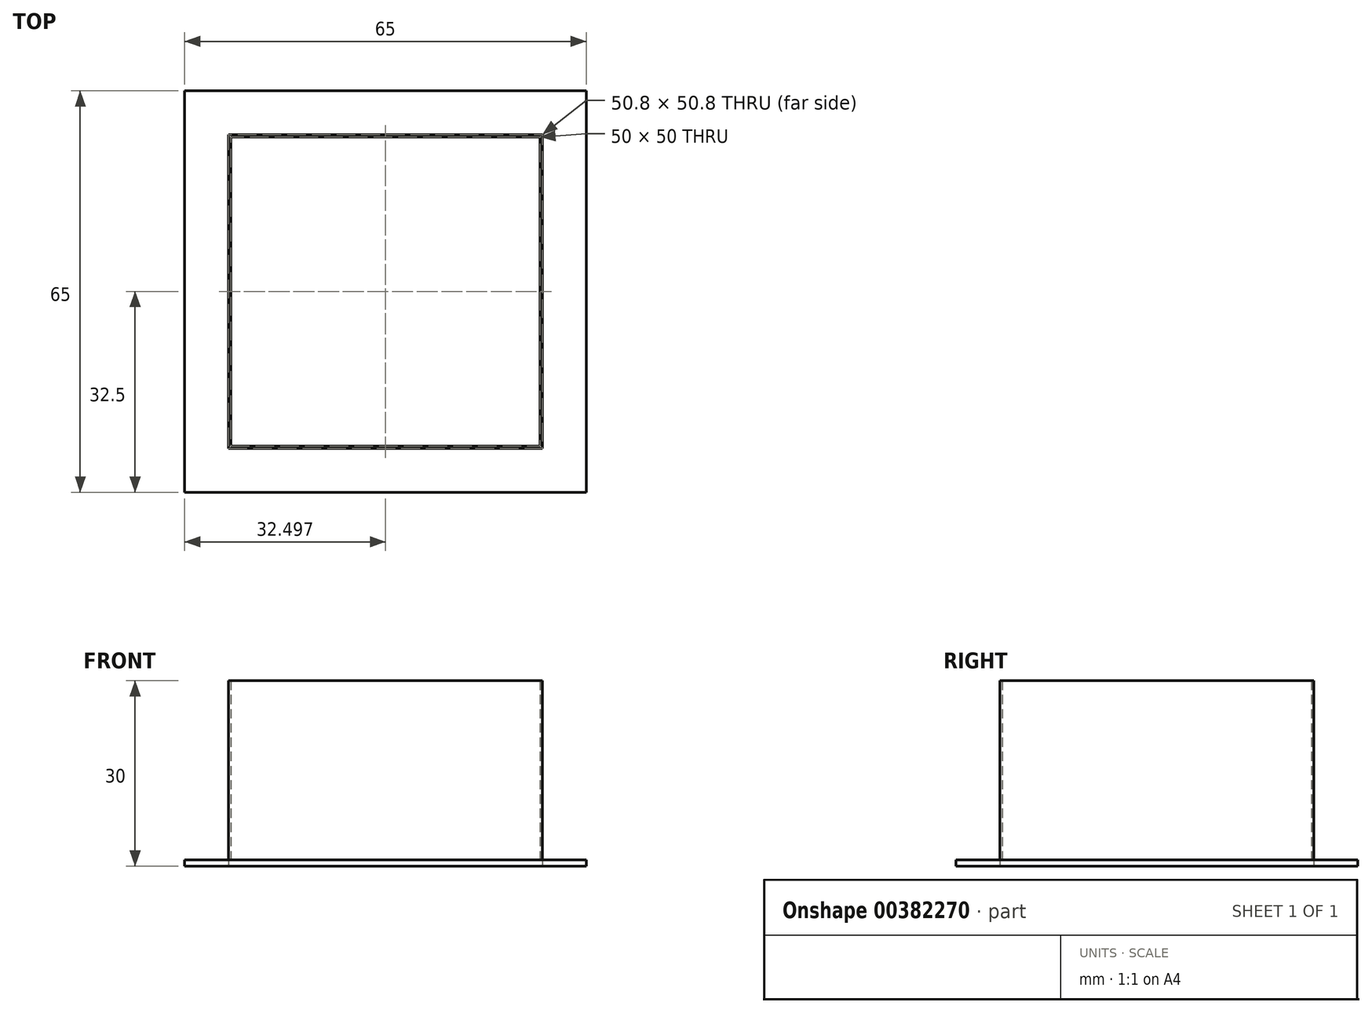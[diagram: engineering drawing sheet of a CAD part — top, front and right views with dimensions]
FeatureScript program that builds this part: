
annotation { "Feature Type Name" : "Feature", "Feature Type Description" : "" }
export const myFeature = defineFeature(function(context is Context, id is Id, definition is map)
    precondition{}
    {
        {
            var Q0;
            Q0=qCreatedBy(makeId("Top.planeOp"),FACE);
            var sketch = newSketch(context, id + "F0", { "sketchPlane" : qUnion([Q0])});
            skLineSegment(sketch, "E0.bottom", {"start": v(-57.14, 25) * mm, "end": v(-7.14, 25) * mm});
            skLineSegment(sketch, "E0.top", {"start": v(-57.14, -25) * mm, "end": v(-7.14, -25) * mm});
            skLineSegment(sketch, "E0.left", {"start": v(-57.14, 25) * mm, "end": v(-57.14, -25) * mm});
            skLineSegment(sketch, "E0.right", {"start": v(-7.14, 25) * mm, "end": v(-7.14, -25) * mm});
            skPoint(sketch, "E0.middle", {"position": v(-32.14, 0) * mm});
            skLineSegment(sketch, "E1.bottom", {"start": v(-57.54, 25.4) * mm, "end": v(-6.74, 25.4) * mm});
            skLineSegment(sketch, "E1.top", {"start": v(-57.54, -25.4) * mm, "end": v(-6.74, -25.4) * mm});
            skLineSegment(sketch, "E1.left", {"start": v(-57.54, 25.4) * mm, "end": v(-57.54, -25.4) * mm});
            skLineSegment(sketch, "E1.right", {"start": v(-6.74, 25.4) * mm, "end": v(-6.74, -25.4) * mm});
            skLineSegment(sketch, "E2.bottom", {"start": v(-64.64, 32.5) * mm, "end": v(0.36, 32.5) * mm});
            skLineSegment(sketch, "E2.top", {"start": v(-64.64, -32.5) * mm, "end": v(0.36, -32.5) * mm});
            skLineSegment(sketch, "E2.left", {"start": v(-64.64, 32.5) * mm, "end": v(-64.64, -32.5) * mm});
            skLineSegment(sketch, "E2.right", {"start": v(0.36, 32.5) * mm, "end": v(0.36, -32.5) * mm});
            skSolve(sketch);
        }
        {
            var Q0;
            Q0=makeQuery(id+"F0.imprint","IMPRINT",FACE,{"disambiguationData":[TD([[makeQuery(id+"F0.imprint","IMPRINT",EDGE,{"derivedFrom":sQuery(id+"F0.wireOp",EDGE,"E0.bottom")}),1.0]])]});
            extrude(context, id + "F1", {"entities" : qUnion([Q0]), "depth" : 30 * mm});
        }
        {
            var Q0;
            Q0=makeQuery(id+"F0.imprint","IMPRINT",FACE,{"disambiguationData":[TD([[makeQuery(id+"F0.imprint","IMPRINT",EDGE,{"derivedFrom":sQuery(id+"F0.wireOp",EDGE,"E1.bottom")}),1.0]])]});
            extrude(context, id + "F2", {"entities" : qUnion([Q0]), "depth" : 1 * mm});
        }
    });
